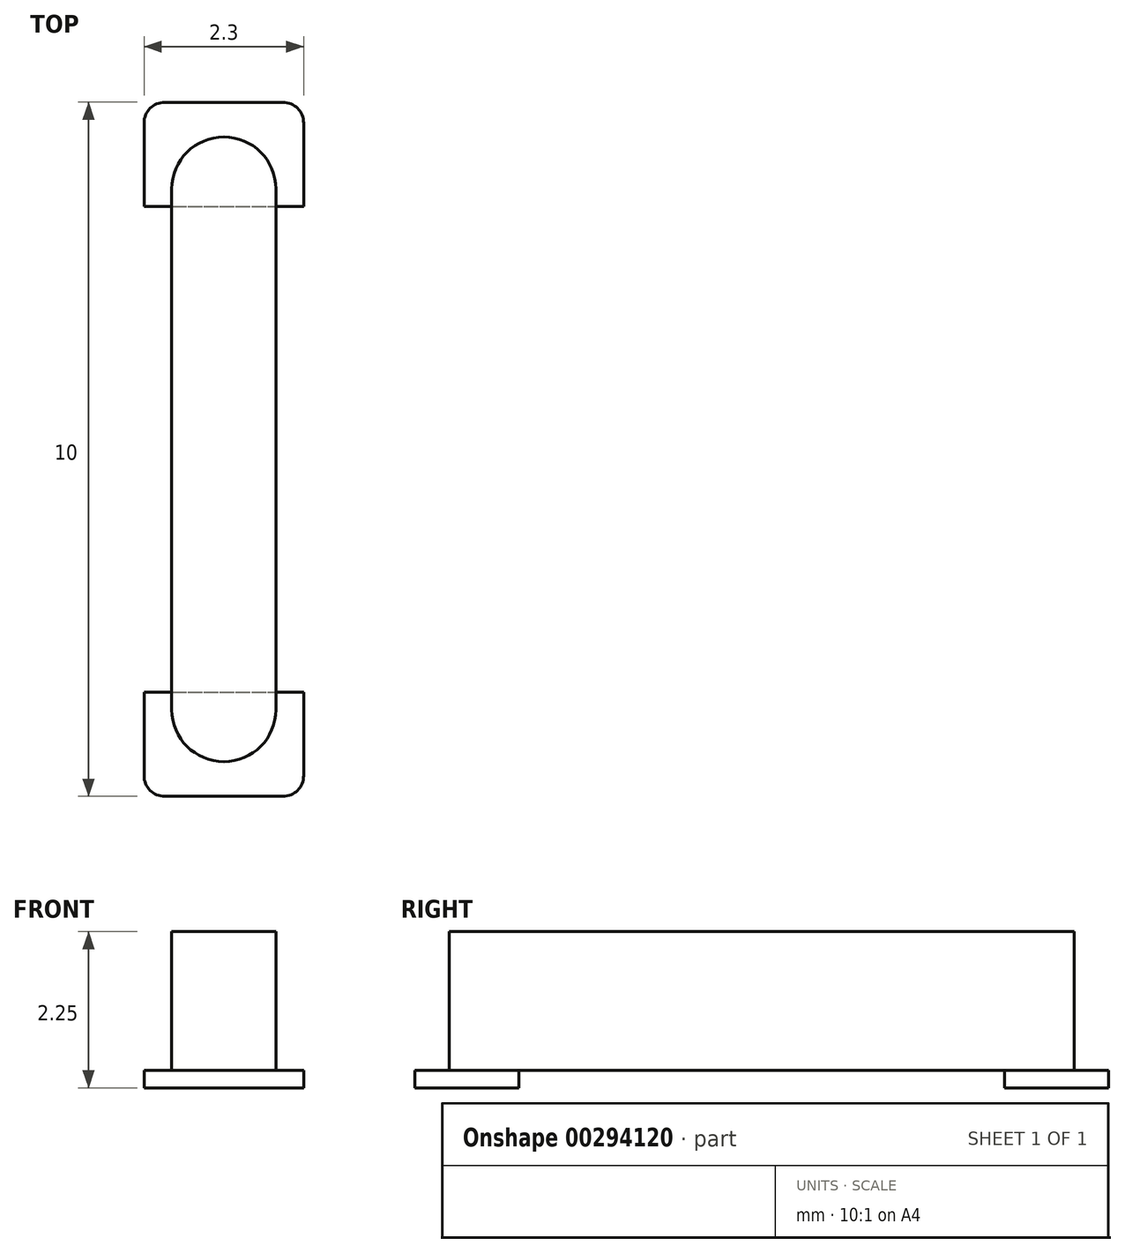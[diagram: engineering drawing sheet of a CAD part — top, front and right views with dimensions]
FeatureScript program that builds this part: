
annotation { "Feature Type Name" : "Feature", "Feature Type Description" : "" }
export const myFeature = defineFeature(function(context is Context, id is Id, definition is map)
    precondition{}
    {
        {
            var Q0;
            Q0=qCreatedBy(makeId("Top.planeOp"),FACE);
            var sketch = newSketch(context, id + "F0", { "sketchPlane" : qUnion([Q0])});
            skLineSegment(sketch, "E0.bottom", {"start": v(-1.5, 9.68) * mm, "end": v(0, 9.68) * mm});
            skLineSegment(sketch, "E0.top", {"start": v(-1.5, 0.68) * mm, "end": v(0, 0.68) * mm});
            skLineSegment(sketch, "E0.left", {"start": v(-1.5, 9.68) * mm, "end": v(-1.5, 0.68) * mm});
            skLineSegment(sketch, "E0.right", {"start": v(0, 9.68) * mm, "end": v(0, 0.68) * mm});
            skPoint(sketch, "E1", {"position": v(-1.5, 5.68) * mm});
            skPoint(sketch, "E2", {"position": v(-1.5, 4.68) * mm});
            skPoint(sketch, "E3.second.point", {"position": v(0, 5.68) * mm});
            skPoint(sketch, "E3.third.point", {"position": v(-0.52, 4.96) * mm});
            skPoint(sketch, "E4.second.point", {"position": v(0, 4.68) * mm});
            skPoint(sketch, "E4.third.point", {"position": v(-0.69, -7.07) * mm});
            skPoint(sketch, "E5", {"position": v(-1.5, 8.68) * mm});
            skPoint(sketch, "E6", {"position": v(-1.5, 1.68) * mm});
            skLineSegment(sketch, "E7.bottom", {"start": v(-1.9, 8.68) * mm, "end": v(0.4, 8.68) * mm});
            skLineSegment(sketch, "E7.top", {"start": v(-1.9, 10.18) * mm, "end": v(0.4, 10.18) * mm});
            skLineSegment(sketch, "E7.left", {"start": v(-1.9, 8.68) * mm, "end": v(-1.9, 10.18) * mm});
            skLineSegment(sketch, "E7.right", {"start": v(0.4, 8.68) * mm, "end": v(0.4, 10.18) * mm});
            skLineSegment(sketch, "E8.bottom", {"start": v(-1.9, 1.68) * mm, "end": v(0.4, 1.68) * mm});
            skLineSegment(sketch, "E8.top", {"start": v(-1.9, 0.18) * mm, "end": v(0.4, 0.18) * mm});
            skLineSegment(sketch, "E8.left", {"start": v(-1.9, 1.68) * mm, "end": v(-1.9, 0.18) * mm});
            skLineSegment(sketch, "E8.right", {"start": v(0.4, 1.68) * mm, "end": v(0.4, 0.18) * mm});
            skSolve(sketch);
        }
        {
            var Q0;
            {var subQ0=sQuery(id+"F0.wireOp",EDGE,"E0.bottom");Q0=makeQuery(id+"F0.imprint","IMPRINT",FACE,{"disambiguationData":[TD([[makeQuery(id+"F0.imprint","IMPRINT",EDGE,{"derivedFrom":subQ0}),-1.0]])]});}
            var Q1;
            {var subQ0=sQuery(id+"F0.wireOp",EDGE,"E7.bottom");var subQ1=sQuery(id+"F0.wireOp",EDGE,"E0.left");var subQ2=makeQuery(id+"F0.imprint","INTERSECT",VERTEX,{"derivedFrom":[subQ1,subQ0]});Q1=makeQuery(id+"F0.imprint","IMPRINT",FACE,{"disambiguationData":[TD([[makeQuery(id+"F0.imprint","IMPRINT",EDGE,{"disambiguationData":[TD([[subQ2,-1.0]])],"derivedFrom":subQ1}),1.0]])]});}
            var Q2;
            {var subQ0=sQuery(id+"F0.wireOp",EDGE,"E3");var subQ1=makeQuery(id+"F0.imprint","INTERSECT",VERTEX,{"derivedFrom":[sQuery(id+"F0.wireOp",EDGE,"E0.left"),subQ0]});Q2=makeQuery(id+"F0.imprint","IMPRINT",FACE,{"disambiguationData":[TD([[makeQuery(id+"F0.imprint","IMPRINT",EDGE,{"disambiguationData":[TD([[subQ1,1.0]])],"derivedFrom":subQ0}),1.0]])]});}
            var Q3;
            {var subQ0=sQuery(id+"F0.wireOp",EDGE,"E3");var subQ1=sQuery(id+"F0.wireOp",EDGE,"E0.left");var subQ2=makeQuery(id+"F0.imprint","INTERSECT",VERTEX,{"derivedFrom":[subQ1,subQ0]});Q3=makeQuery(id+"F0.imprint","IMPRINT",FACE,{"disambiguationData":[TD([[makeQuery(id+"F0.imprint","IMPRINT",EDGE,{"disambiguationData":[TD([[subQ2,-1.0]])],"derivedFrom":subQ1}),1.0]])]});}
            var Q4;
            {var subQ0=sQuery(id+"F0.wireOp",EDGE,"E4");var subQ1=makeQuery(id+"F0.imprint","INTERSECT",VERTEX,{"derivedFrom":[sQuery(id+"F0.wireOp",EDGE,"E0.left"),subQ0]});Q4=makeQuery(id+"F0.imprint","IMPRINT",FACE,{"disambiguationData":[TD([[makeQuery(id+"F0.imprint","IMPRINT",EDGE,{"disambiguationData":[TD([[subQ1,1.0]])],"derivedFrom":subQ0}),1.0]])]});}
            var Q5;
            {var subQ0=sQuery(id+"F0.wireOp",EDGE,"E4");var subQ1=sQuery(id+"F0.wireOp",EDGE,"E0.left");var subQ2=makeQuery(id+"F0.imprint","INTERSECT",VERTEX,{"derivedFrom":[subQ1,subQ0]});Q5=makeQuery(id+"F0.imprint","IMPRINT",FACE,{"disambiguationData":[TD([[makeQuery(id+"F0.imprint","IMPRINT",EDGE,{"disambiguationData":[TD([[subQ2,-1.0]])],"derivedFrom":subQ1}),1.0]])]});}
            var Q6;
            {var subQ0=sQuery(id+"F0.wireOp",EDGE,"E0.top");Q6=makeQuery(id+"F0.imprint","IMPRINT",FACE,{"disambiguationData":[TD([[makeQuery(id+"F0.imprint","IMPRINT",EDGE,{"derivedFrom":subQ0}),1.0]])]});}
            extrude(context, id + "F1", {"entities" : qUnion([Q0, Q1, Q2, Q3, Q4, Q5, Q6]), "depth" : 2 * mm});
        }
        {
            var Q0;
            {var subQ0=sQuery(id+"F0.wireOp",EDGE,"E0.top");Q0=makeQuery(id+"F0.imprint","IMPRINT",FACE,{"disambiguationData":[TD([[makeQuery(id+"F0.imprint","IMPRINT",EDGE,{"derivedFrom":subQ0}),1.0]])]});}
            var Q1;
            {var subQ5=sQuery(id+"F0.wireOp",EDGE,"E0.top");Q1=makeQuery(id+"F0.imprint","IMPRINT",FACE,{"disambiguationData":[TD([[makeQuery(id+"F0.imprint","IMPRINT",EDGE,{"derivedFrom":subQ5}),-1.0]])]});}
            var Q2;
            {var subQ5=sQuery(id+"F0.wireOp",EDGE,"E0.bottom");Q2=makeQuery(id+"F0.imprint","IMPRINT",FACE,{"disambiguationData":[TD([[makeQuery(id+"F0.imprint","IMPRINT",EDGE,{"derivedFrom":subQ5}),1.0]])]});}
            var Q3;
            {var subQ0=sQuery(id+"F0.wireOp",EDGE,"E0.bottom");Q3=makeQuery(id+"F0.imprint","IMPRINT",FACE,{"disambiguationData":[TD([[makeQuery(id+"F0.imprint","IMPRINT",EDGE,{"derivedFrom":subQ0}),-1.0]])]});}
            extrude(context, id + "F2", {"entities" : qUnion([Q0, Q1, Q2, Q3]), "operationType" : NewBodyOperationType.ADD, "oppositeDirection" : true, "depth" : 0.25 * mm});
        }
        {
            var Q0;
            Q0=makeQuery(id+"F1.opExtrude","SWEPT_EDGE",EDGE,{"disambiguationData":[OSD([sQuery(id+"F0.wireOp",EDGE,"E0.bottom"),sQuery(id+"F0.wireOp",EDGE,"E0.right")])]});
            var Q1;
            Q1=makeQuery(id+"F1.opExtrude","SWEPT_EDGE",EDGE,{"disambiguationData":[OSD([sQuery(id+"F0.wireOp",EDGE,"E0.bottom"),sQuery(id+"F0.wireOp",EDGE,"E0.left")])]});
            var Q2;
            Q2=makeQuery(id+"F1.opExtrude","SWEPT_EDGE",EDGE,{"disambiguationData":[OSD([sQuery(id+"F0.wireOp",EDGE,"E0.top"),sQuery(id+"F0.wireOp",EDGE,"E0.right")])]});
            var Q3;
            Q3=makeQuery(id+"F1.opExtrude","SWEPT_EDGE",EDGE,{"disambiguationData":[OSD([sQuery(id+"F0.wireOp",EDGE,"E0.top"),sQuery(id+"F0.wireOp",EDGE,"E0.left")])]});
            fillet(context, id + "F3", {"entities" : qUnion([Q0, Q1, Q2, Q3]), "radius" : 0.75 * mm, "tangentPropagation" : true, "allowEdgeOverflow" : false});
        }
        {
            var Q0;
            Q0=makeQuery(id+"F2.opExtrude","SWEPT_EDGE",EDGE,{"disambiguationData":[OSD([sQuery(id+"F0.wireOp",EDGE,"E7.top"),sQuery(id+"F0.wireOp",EDGE,"E7.right")])]});
            var Q1;
            Q1=makeQuery(id+"F2.opExtrude","SWEPT_EDGE",EDGE,{"disambiguationData":[OSD([sQuery(id+"F0.wireOp",EDGE,"E7.top"),sQuery(id+"F0.wireOp",EDGE,"E7.left")])]});
            var Q2;
            Q2=makeQuery(id+"F2.opExtrude","SWEPT_EDGE",EDGE,{"disambiguationData":[OSD([sQuery(id+"F0.wireOp",EDGE,"E8.top"),sQuery(id+"F0.wireOp",EDGE,"E8.right")])]});
            var Q3;
            Q3=makeQuery(id+"F2.opExtrude","SWEPT_EDGE",EDGE,{"disambiguationData":[OSD([sQuery(id+"F0.wireOp",EDGE,"E8.top"),sQuery(id+"F0.wireOp",EDGE,"E8.left")])]});
            fillet(context, id + "F4", {"entities" : qUnion([Q0, Q1, Q2, Q3]), "radius" : 0.3 * mm, "tangentPropagation" : true, "allowEdgeOverflow" : false});
        }
    });
